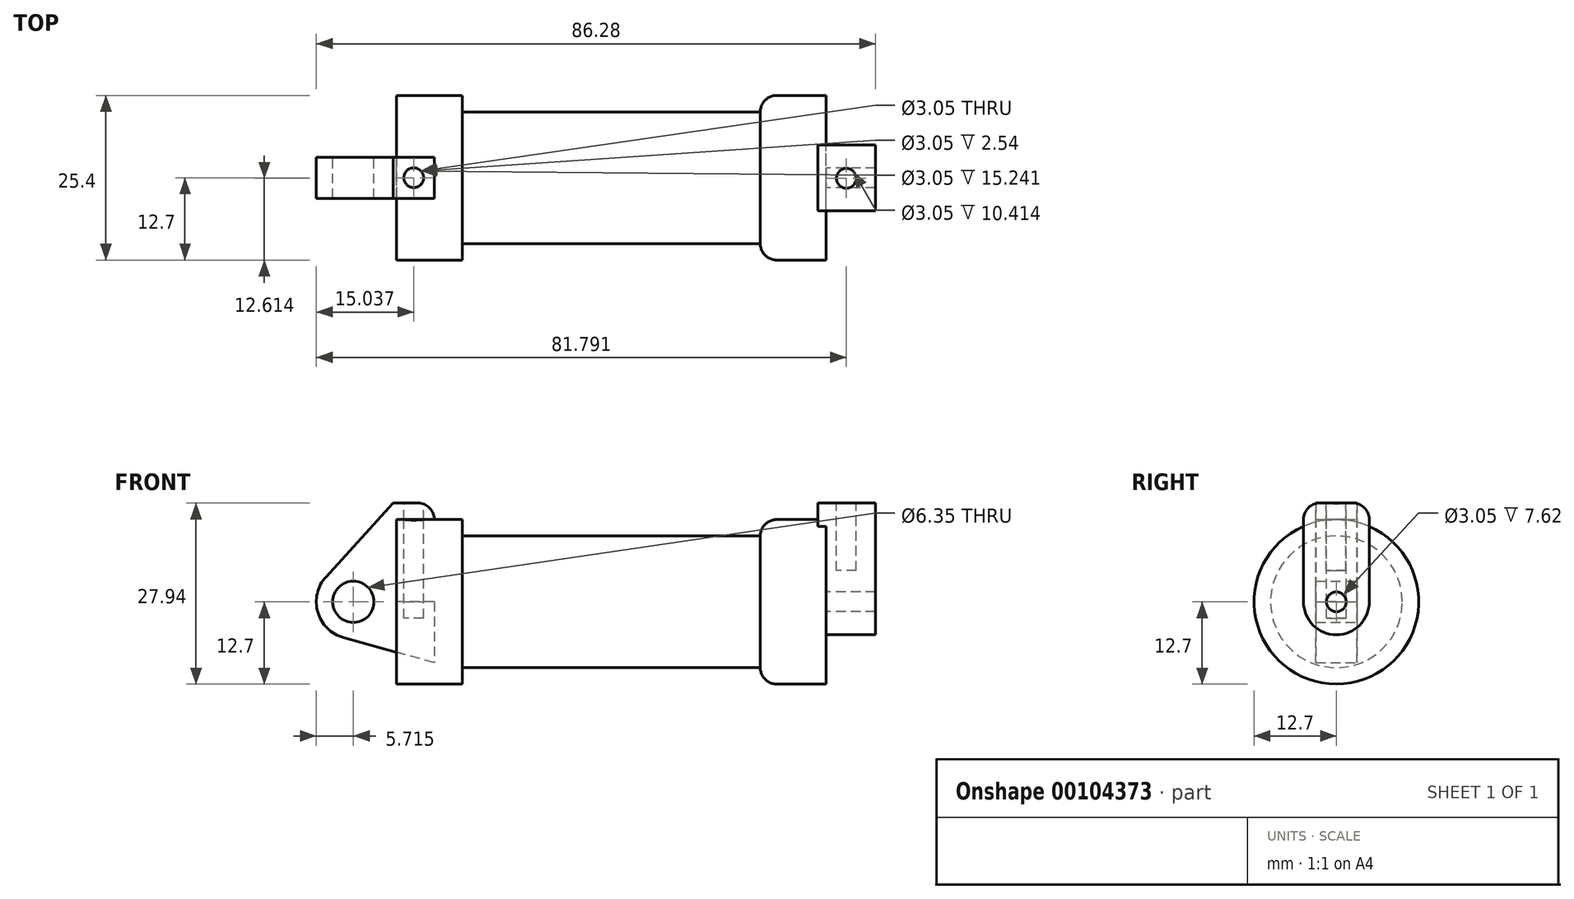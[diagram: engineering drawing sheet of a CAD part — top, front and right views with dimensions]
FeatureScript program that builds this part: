
annotation { "Feature Type Name" : "Feature", "Feature Type Description" : "" }
export const myFeature = defineFeature(function(context is Context, id is Id, definition is map)
    precondition{}
    {
        {
            var Q0;
            Q0=qCreatedBy(makeId("Front.planeOp"),FACE);
            var sketch = newSketch(context, id + "F0", { "sketchPlane" : qUnion([Q0])});
            skLineSegment(sketch, "E0", {"start": v(0, 0) * mm, "end": v(0, 12.7) * mm});
            skLineSegment(sketch, "E1", {"start": v(0, 12.7) * mm, "end": v(10.16, 12.7) * mm});
            skLineSegment(sketch, "E2", {"start": v(10.16, 12.7) * mm, "end": v(10.16, 10.16) * mm});
            skLineSegment(sketch, "E3", {"start": v(10.16, 10.16) * mm, "end": v(56.13, 10.16) * mm});
            skLineSegment(sketch, "E4", {"start": v(56.13, 10.16) * mm, "end": v(56.13, 10.16) * mm});
            skLineSegment(sketch, "E5", {"start": v(58.67, 12.7) * mm, "end": v(66.3, 12.7) * mm});
            skLineSegment(sketch, "E6", {"start": v(66.3, 12.7) * mm, "end": v(66.3, 0) * mm});
            skLineSegment(sketch, "E7", {"start": v(66.3, 0) * mm, "end": v(0, 0) * mm});
            skLineSegment(sketch, "E8", {"start": v(3.3, 15.24) * mm, "end": v(-0.5, 15.24) * mm});
            skLineSegment(sketch, "E9", {"start": v(-0.5, 15.24) * mm, "end": v(-10.88, 3.85) * mm});
            skLineSegment(sketch, "E10", {"start": v(0, 0) * mm, "end": v(-6.65, 0) * mm});
            skCircle(sketch, "E11", {"center": v(-6.65, 0) * mm, "radius": 5.72 * mm});
            skCircle(sketch, "E12", {"center": v(-6.65, 0) * mm, "radius": 3.18 * mm});
            skLineSegment(sketch, "E13", {"start": v(5.84, 12.7) * mm, "end": v(5.84, -9.4) * mm});
            skLineSegment(sketch, "E14", {"start": v(5.84, -9.4) * mm, "end": v(-8.18, -5.5) * mm});
            skPoint(sketch, "E15.visualSharp", {"position": v(5.84, 15.24) * mm});
            skArc(sketch, "E15.filletArc", {"start": v(5.84, 12.7) * mm, "mid": v(5.1, 14.5) * mm, "end": v(3.3, 15.24) * mm});
            skPoint(sketch, "E16.visualSharp", {"position": v(56.13, 12.7) * mm});
            skArc(sketch, "E16.filletArc", {"start": v(58.67, 12.7) * mm, "mid": v(56.88, 11.96) * mm, "end": v(56.13, 10.16) * mm});
            skSolve(sketch);
        }
        {
            var Q0;
            {var subQ0=sQuery(id+"F0.wireOp",EDGE,"E0");Q0=makeQuery(id+"F0.imprint","IMPRINT",FACE,{"disambiguationData":[TD([[makeQuery(id+"F0.imprint","IMPRINT",EDGE,{"derivedFrom":subQ0}),-1.0]])]});}
            var Q1;
            {var subQ0=sQuery(id+"F0.wireOp",EDGE,"E2");Q1=makeQuery(id+"F0.imprint","IMPRINT",FACE,{"disambiguationData":[TD([[makeQuery(id+"F0.imprint","IMPRINT",EDGE,{"derivedFrom":subQ0}),-1.0]])]});}
            var Q2;
            Q2=sQuery(id+"F0.wireOp",EDGE,"E7");
            revolve(context, id + "F1", {"entities" : qUnion([Q0, Q1]), "axis" : qUnion([Q2]), "revolveType" : RevolveType.FULL});
        }
        {
            var Q0;
            {var subQ3=sQuery(id+"F0.wireOp",EDGE,"E0");Q0=makeQuery(id+"F0.imprint","IMPRINT",FACE,{"disambiguationData":[TD([[makeQuery(id+"F0.imprint","IMPRINT",EDGE,{"derivedFrom":subQ3}),1.0]])]});}
            var Q1;
            {var subQ0=sQuery(id+"F0.wireOp",EDGE,"E14");Q1=makeQuery(id+"F0.imprint","IMPRINT",FACE,{"disambiguationData":[TD([[makeQuery(id+"F0.imprint","IMPRINT",EDGE,{"derivedFrom":subQ0}),-1.0]])]});}
            var Q2;
            {var subQ4=sQuery(id+"F0.wireOp",EDGE,"E12");Q2=makeQuery(id+"F0.imprint","IMPRINT",FACE,{"disambiguationData":[TD([[makeQuery(id+"F0.imprint","IMPRINT",EDGE,{"derivedFrom":subQ4}),-1.0]])]});}
            extrude(context, id + "F2", {"entities" : qUnion([Q0, Q1, Q2]), "endBound" : BoundingType.SYMMETRIC, "depth" : 6.35 * mm});
        }
        {
            var Q0;
            Q0=makeQuery(id+"F1.opRevolve","SWEPT_FACE",FACE,{"disambiguationData":[OSD([sQuery(id+"F0.wireOp",EDGE,"E6")])]});
            var sketch = newSketch(context, id + "F3", { "sketchPlane" : qUnion([Q0])});
            skCircle(sketch, "E17", {"center": v(0, 0) * mm, "radius": 1.52 * mm});
            skCircle(sketch, "E18", {"center": v(0, 0) * mm, "radius": 5.08 * mm});
            skLineSegment(sketch, "E19", {"start": v(5.08, 0) * mm, "end": v(5.08, 12.7) * mm});
            skLineSegment(sketch, "E20", {"start": v(-5.08, 0) * mm, "end": v(-5.08, 12.7) * mm});
            skLineSegment(sketch, "E21", {"start": v(-2.54, 15.24) * mm, "end": v(2.54, 15.24) * mm});
            skPoint(sketch, "E22.visualSharp", {"position": v(-5.08, 15.24) * mm});
            skArc(sketch, "E22.filletArc", {"start": v(-2.54, 15.24) * mm, "mid": v(-4.34, 14.5) * mm, "end": v(-5.08, 12.7) * mm});
            skPoint(sketch, "E23.visualSharp", {"position": v(5.08, 15.24) * mm});
            skArc(sketch, "E23.filletArc", {"start": v(5.08, 12.7) * mm, "mid": v(4.34, 14.5) * mm, "end": v(2.54, 15.24) * mm});
            skSolve(sketch);
        }
        {
            var Q0;
            {var subQ0=sQuery(id+"F3.wireOp",EDGE,"E21");Q0=makeQuery(id+"F3.imprint","IMPRINT",FACE,{"disambiguationData":[TD([[makeQuery(id+"F3.imprint","IMPRINT",EDGE,{"derivedFrom":subQ0}),-1.0]])]});}
            var Q1;
            {var subQ0=sQuery(id+"F3.wireOp",EDGE,"E19");var subQ1=sQuery(id+"F3.wireOp",EDGE,"E18");var subQ2=makeQuery(id+"F3.imprint","INTERSECT",VERTEX,{"derivedFrom":[subQ1,subQ0]});Q1=makeQuery(id+"F3.imprint","IMPRINT",FACE,{"disambiguationData":[TD([[makeQuery(id+"F3.imprint","IMPRINT",EDGE,{"disambiguationData":[TD([[subQ2,-1.0]])],"derivedFrom":subQ1}),-1.0]])]});}
            var Q2;
            Q2=makeQuery(id+"F3.imprint","IMPRINT",FACE,{"disambiguationData":[TD([[makeQuery(id+"F3.imprint","IMPRINT",EDGE,{"derivedFrom":sQuery(id+"F3.wireOp",EDGE,"E17")}),-1.0]])]});
            extrude(context, id + "F4", {"entities" : qUnion([Q0, Q1, Q2]), "operationType" : NewBodyOperationType.ADD, "depth" : 7.62 * mm});
        }
        {
            var Q0;
            Q0=makeQuery(id+"F4.opExtrude","CAP_FACE",FACE,{"disambiguationData":[OSD([sQuery(id+"F3.wireOp",EDGE,"E17"),sQuery(id+"F3.wireOp",EDGE,"E18"),sQuery(id+"F3.wireOp",EDGE,"E19"),sQuery(id+"F3.wireOp",EDGE,"E20"),sQuery(id+"F3.wireOp",EDGE,"E21")])],"isStart":true});
            extrude(context, id + "F5", {"entities" : qUnion([Q0]), "operationType" : NewBodyOperationType.ADD, "depth" : 1.27 * mm});
        }
        {
            var Q0;
            Q0=makeQuery(id+"F2.opExtrude","SWEPT_FACE",FACE,{"disambiguationData":[OSD([sQuery(id+"F0.wireOp",EDGE,"E8")])]});
            var sketch = newSketch(context, id + "F6", { "sketchPlane" : qUnion([Q0])});
            skCircle(sketch, "E24", {"center": v(2.67, 0) * mm, "radius": 1.52 * mm});
            skCircle(sketch, "E25", {"center": v(69.42, -0.09) * mm, "radius": 1.52 * mm});
            skSolve(sketch);
        }
        {
            var Q0;
            Q0=makeQuery(id+"F6.imprint","IMPRINT",FACE,{"disambiguationData":[TD([[makeQuery(id+"F6.imprint","IMPRINT",EDGE,{"derivedFrom":sQuery(id+"F6.wireOp",EDGE,"E24")}),1.0]])]});
            extrude(context, id + "F7", {"entities" : qUnion([Q0]), "operationType" : NewBodyOperationType.REMOVE, "oppositeDirection" : true, "depth" : 17.78 * mm});
        }
        {
            var Q0;
            Q0=makeQuery(id+"F6.imprint","IMPRINT",FACE,{"disambiguationData":[TD([[makeQuery(id+"F6.imprint","IMPRINT",EDGE,{"derivedFrom":sQuery(id+"F6.wireOp",EDGE,"E25")}),1.0]])]});
            extrude(context, id + "F8", {"entities" : qUnion([Q0]), "operationType" : NewBodyOperationType.REMOVE, "oppositeDirection" : true, "depth" : 10.4 * mm});
        }
    });
